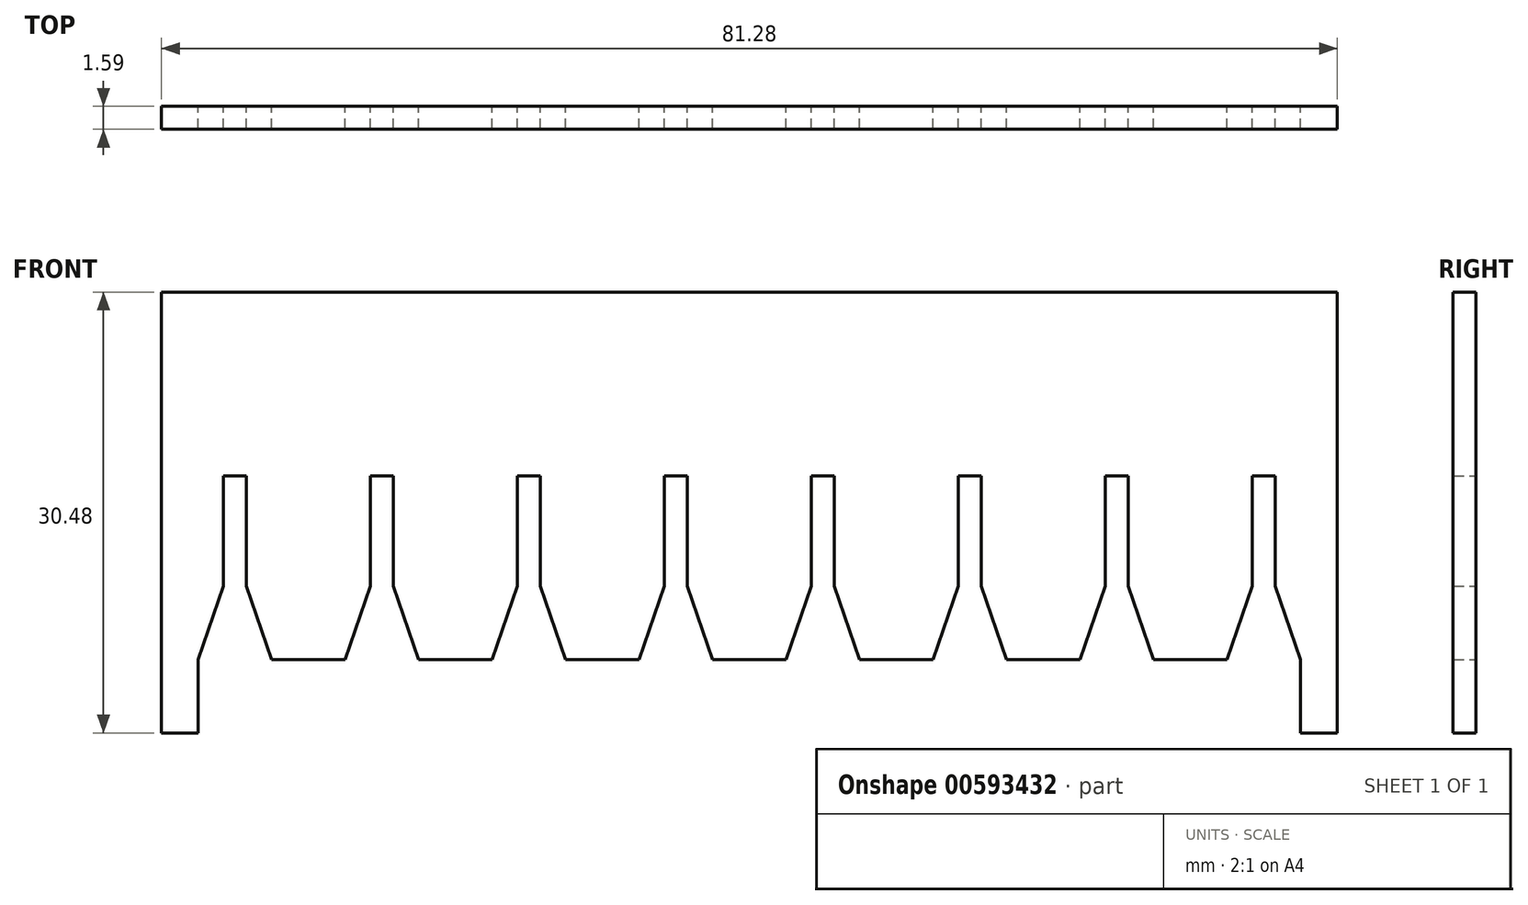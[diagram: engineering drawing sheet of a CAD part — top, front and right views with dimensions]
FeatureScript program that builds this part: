
annotation { "Feature Type Name" : "Feature", "Feature Type Description" : "" }
export const myFeature = defineFeature(function(context is Context, id is Id, definition is map)
    precondition{}
    {
        {
            var Q0;
            Q0=qCreatedBy(makeId("Front.planeOp"),FACE);
            var sketch = newSketch(context, id + "F0", { "sketchPlane" : qUnion([Q0])});
            skLineSegment(sketch, "E0.bottom", {"start": v(0, 0) * mm, "end": v(152.4, 0) * mm});
            skLineSegment(sketch, "E0.top", {"start": v(0, 25.4) * mm, "end": v(152.4, 25.4) * mm});
            skLineSegment(sketch, "E0.left", {"start": v(0, 0) * mm, "end": v(0, 25.4) * mm});
            skLineSegment(sketch, "E0.right", {"start": v(152.4, 0) * mm, "end": v(152.4, 25.4) * mm});
            skSolve(sketch);
        }
        {
            var Q0;
            Q0 = qSketchRegion(id + "F0", true);
            extrude(context, id + "F1", {"entities" : qUnion([Q0]), "depth" : 1.59 * mm, "offsetDistance" : 25.4 * mm});
        }
        {
            var Q0;
            Q0=qCreatedBy(makeId("Front.planeOp"),FACE);
            var sketch = newSketch(context, id + "F2", { "sketchPlane" : qUnion([Q0])});
            skLineSegment(sketch, "E1", {"start": v(2.54, 0) * mm, "end": v(4.3, 5.08) * mm});
            skLineSegment(sketch, "E2", {"start": v(4.3, 5.08) * mm, "end": v(4.3, 12.7) * mm});
            skLineSegment(sketch, "E3", {"start": v(4.3, 12.7) * mm, "end": v(5.87, 12.7) * mm});
            skLineSegment(sketch, "E4", {"start": v(5.87, 12.7) * mm, "end": v(5.87, 5.08) * mm});
            skLineSegment(sketch, "E5", {"start": v(5.87, 5.08) * mm, "end": v(7.62, 0) * mm});
            skLineSegment(sketch, "E6", {"start": v(7.62, 0) * mm, "end": v(2.54, 0) * mm});
            skLineSegment(sketch, "E7", {"start": v(5.08, 12.7) * mm, "end": v(5.08, 0) * mm, "construction": true});
            skLineSegment(sketch, "E8.1.0.0", {"start": v(12.7, 0) * mm, "end": v(14.45, 5.08) * mm});
            skLineSegment(sketch, "E8.1.0.1", {"start": v(16.03, 12.7) * mm, "end": v(16.03, 5.08) * mm});
            skLineSegment(sketch, "E8.1.0.2", {"start": v(14.45, 5.08) * mm, "end": v(14.45, 12.7) * mm});
            skLineSegment(sketch, "E8.1.0.3", {"start": v(16.03, 5.08) * mm, "end": v(17.78, 0) * mm});
            skLineSegment(sketch, "E8.1.0.4", {"start": v(15.24, 12.7) * mm, "end": v(15.24, 0) * mm, "construction": true});
            skLineSegment(sketch, "E8.1.0.5", {"start": v(17.78, 0) * mm, "end": v(12.7, 0) * mm});
            skLineSegment(sketch, "E8.1.0.6", {"start": v(14.45, 12.7) * mm, "end": v(16.03, 12.7) * mm});
            skLineSegment(sketch, "E8.2.0.0", {"start": v(22.86, 0) * mm, "end": v(24.61, 5.08) * mm});
            skLineSegment(sketch, "E8.2.0.1", {"start": v(26.19, 12.7) * mm, "end": v(26.19, 5.08) * mm});
            skLineSegment(sketch, "E8.2.0.2", {"start": v(24.61, 5.08) * mm, "end": v(24.61, 12.7) * mm});
            skLineSegment(sketch, "E8.2.0.3", {"start": v(26.19, 5.08) * mm, "end": v(27.94, 0) * mm});
            skLineSegment(sketch, "E8.2.0.4", {"start": v(25.4, 12.7) * mm, "end": v(25.4, 0) * mm, "construction": true});
            skLineSegment(sketch, "E8.2.0.5", {"start": v(27.94, 0) * mm, "end": v(22.86, 0) * mm});
            skLineSegment(sketch, "E8.2.0.6", {"start": v(24.61, 12.7) * mm, "end": v(26.19, 12.7) * mm});
            skLineSegment(sketch, "E8.3.0.0", {"start": v(33.02, 0) * mm, "end": v(34.77, 5.08) * mm});
            skLineSegment(sketch, "E8.3.0.1", {"start": v(36.35, 12.7) * mm, "end": v(36.35, 5.08) * mm});
            skLineSegment(sketch, "E8.3.0.2", {"start": v(34.77, 5.08) * mm, "end": v(34.77, 12.7) * mm});
            skLineSegment(sketch, "E8.3.0.3", {"start": v(36.35, 5.08) * mm, "end": v(38.1, 0) * mm});
            skLineSegment(sketch, "E8.3.0.4", {"start": v(35.56, 12.7) * mm, "end": v(35.56, 0) * mm, "construction": true});
            skLineSegment(sketch, "E8.3.0.5", {"start": v(38.1, 0) * mm, "end": v(33.02, 0) * mm});
            skLineSegment(sketch, "E8.3.0.6", {"start": v(34.77, 12.7) * mm, "end": v(36.35, 12.7) * mm});
            skLineSegment(sketch, "E8.4.0.0", {"start": v(43.18, 0) * mm, "end": v(44.93, 5.08) * mm});
            skLineSegment(sketch, "E8.4.0.1", {"start": v(46.5, 12.7) * mm, "end": v(46.5, 5.08) * mm});
            skLineSegment(sketch, "E8.4.0.2", {"start": v(44.93, 5.08) * mm, "end": v(44.93, 12.7) * mm});
            skLineSegment(sketch, "E8.4.0.3", {"start": v(46.5, 5.08) * mm, "end": v(48.26, 0) * mm});
            skLineSegment(sketch, "E8.4.0.4", {"start": v(45.72, 12.7) * mm, "end": v(45.72, 0) * mm, "construction": true});
            skLineSegment(sketch, "E8.4.0.5", {"start": v(48.26, 0) * mm, "end": v(43.18, 0) * mm});
            skLineSegment(sketch, "E8.4.0.6", {"start": v(44.93, 12.7) * mm, "end": v(46.5, 12.7) * mm});
            skLineSegment(sketch, "E8.5.0.0", {"start": v(53.34, 0) * mm, "end": v(55.1, 5.08) * mm});
            skLineSegment(sketch, "E8.5.0.1", {"start": v(56.67, 12.7) * mm, "end": v(56.67, 5.08) * mm});
            skLineSegment(sketch, "E8.5.0.2", {"start": v(55.1, 5.08) * mm, "end": v(55.1, 12.7) * mm});
            skLineSegment(sketch, "E8.5.0.3", {"start": v(56.67, 5.08) * mm, "end": v(58.42, 0) * mm});
            skLineSegment(sketch, "E8.5.0.4", {"start": v(55.88, 12.7) * mm, "end": v(55.88, 0) * mm, "construction": true});
            skLineSegment(sketch, "E8.5.0.5", {"start": v(58.42, 0) * mm, "end": v(53.34, 0) * mm});
            skLineSegment(sketch, "E8.5.0.6", {"start": v(55.1, 12.7) * mm, "end": v(56.67, 12.7) * mm});
            skLineSegment(sketch, "E8.direction1", {"start": v(2.54, 0) * mm, "end": v(12.7, 0) * mm, "construction": true});
            skLineSegment(sketch, "E9.0.6.0", {"start": v(63.5, 0) * mm, "end": v(65.25, 5.08) * mm});
            skLineSegment(sketch, "E9.3.6.0", {"start": v(66.83, 12.7) * mm, "end": v(66.83, 5.08) * mm});
            skLineSegment(sketch, "E9.6.6.0", {"start": v(65.25, 5.08) * mm, "end": v(65.25, 12.7) * mm});
            skLineSegment(sketch, "E9.9.6.0", {"start": v(66.83, 5.08) * mm, "end": v(68.58, 0) * mm});
            skLineSegment(sketch, "E9.12.6.0", {"start": v(66.04, 12.7) * mm, "end": v(66.04, 0) * mm, "construction": true});
            skLineSegment(sketch, "E9.15.6.0", {"start": v(68.58, 0) * mm, "end": v(63.5, 0) * mm});
            skLineSegment(sketch, "E9.18.6.0", {"start": v(65.25, 12.7) * mm, "end": v(66.83, 12.7) * mm});
            skLineSegment(sketch, "E9.0.7.0", {"start": v(73.66, 0) * mm, "end": v(75.41, 5.08) * mm});
            skLineSegment(sketch, "E9.3.7.0", {"start": v(76.99, 12.7) * mm, "end": v(76.99, 5.08) * mm});
            skLineSegment(sketch, "E9.6.7.0", {"start": v(75.41, 5.08) * mm, "end": v(75.41, 12.7) * mm});
            skLineSegment(sketch, "E9.9.7.0", {"start": v(76.99, 5.08) * mm, "end": v(78.74, 0) * mm});
            skLineSegment(sketch, "E9.12.7.0", {"start": v(76.2, 12.7) * mm, "end": v(76.2, 0) * mm, "construction": true});
            skLineSegment(sketch, "E9.15.7.0", {"start": v(78.74, 0) * mm, "end": v(73.66, 0) * mm});
            skLineSegment(sketch, "E9.18.7.0", {"start": v(75.41, 12.7) * mm, "end": v(76.99, 12.7) * mm});
            skSolve(sketch);
        }
        {
            var Q0;
            Q0 = qSketchRegion(id + "F2", true);
            extrude(context, id + "F3", {"entities" : qUnion([Q0]), "operationType" : NewBodyOperationType.REMOVE, "endBound" : BoundingType.THROUGH_ALL, "depth" : 25.4 * mm, "offsetDistance" : 25.4 * mm});
        }
        {
            var Q0;
            Q0=makeQuery(id+"F1.opExtrude","CAP_FACE",FACE,{"disambiguationData":[OSD([sQuery(id+"F0.wireOp",EDGE,"E0.bottom"),sQuery(id+"F0.wireOp",EDGE,"E0.top"),sQuery(id+"F0.wireOp",EDGE,"E0.left"),sQuery(id+"F0.wireOp",EDGE,"E0.right")])],"isStart":false});
            var sketch = newSketch(context, id + "F4", { "sketchPlane" : qUnion([Q0])});
            skLineSegment(sketch, "E10.bottom", {"start": v(152.4, 25.4) * mm, "end": v(81.28, 25.4) * mm});
            skLineSegment(sketch, "E10.top", {"start": v(152.4, 0) * mm, "end": v(81.28, 0) * mm});
            skLineSegment(sketch, "E10.left", {"start": v(152.4, 25.4) * mm, "end": v(152.4, 0) * mm});
            skLineSegment(sketch, "E10.right", {"start": v(81.28, 25.4) * mm, "end": v(81.28, 0) * mm});
            skSolve(sketch);
        }
        {
            var Q0;
            Q0 = qSketchRegion(id + "F4", true);
            extrude(context, id + "F5", {"entities" : qUnion([Q0]), "operationType" : NewBodyOperationType.REMOVE, "endBound" : BoundingType.THROUGH_ALL, "oppositeDirection" : true, "depth" : 25.4 * mm, "offsetDistance" : 25.4 * mm});
        }
        {
            var Q0;
            Q0=makeQuery(id+"F1.opExtrude","CAP_FACE",FACE,{"disambiguationData":[OSD([sQuery(id+"F0.wireOp",EDGE,"E0.bottom"),sQuery(id+"F0.wireOp",EDGE,"E0.top"),sQuery(id+"F0.wireOp",EDGE,"E0.left"),sQuery(id+"F0.wireOp",EDGE,"E0.right")])],"isStart":false});
            var sketch = newSketch(context, id + "F6", { "sketchPlane" : qUnion([Q0])});
            skLineSegment(sketch, "E11.bottom", {"start": v(0, 0) * mm, "end": v(2.54, 0) * mm});
            skLineSegment(sketch, "E11.top", {"start": v(0, -5.08) * mm, "end": v(2.54, -5.08) * mm});
            skLineSegment(sketch, "E11.left", {"start": v(0, 0) * mm, "end": v(0, -5.08) * mm});
            skLineSegment(sketch, "E11.right", {"start": v(2.54, 0) * mm, "end": v(2.54, -5.08) * mm});
            skLineSegment(sketch, "E12.bottom", {"start": v(81.28, 0) * mm, "end": v(78.74, 0) * mm});
            skLineSegment(sketch, "E12.top", {"start": v(81.28, -5.08) * mm, "end": v(78.74, -5.08) * mm});
            skLineSegment(sketch, "E12.left", {"start": v(81.28, 0) * mm, "end": v(81.28, -5.08) * mm});
            skLineSegment(sketch, "E12.right", {"start": v(78.74, 0) * mm, "end": v(78.74, -5.08) * mm});
            skSolve(sketch);
        }
        {
            var Q0;
            Q0 = qSketchRegion(id + "F6", true);
            var Q1;
            Q1=makeQuery(id+"F1.opExtrude","CAP_FACE",FACE,{"disambiguationData":[OSD([sQuery(id+"F0.wireOp",EDGE,"E0.bottom"),sQuery(id+"F0.wireOp",EDGE,"E0.top"),sQuery(id+"F0.wireOp",EDGE,"E0.left"),sQuery(id+"F0.wireOp",EDGE,"E0.right")])],"isStart":true});
            extrude(context, id + "F7", {"entities" : qUnion([Q0]), "operationType" : NewBodyOperationType.ADD, "endBound" : BoundingType.UP_TO_SURFACE, "oppositeDirection" : true, "depth" : 25.4 * mm, "endBoundEntityFace" : qUnion([Q1]), "offsetDistance" : 25.4 * mm});
        }
    });
